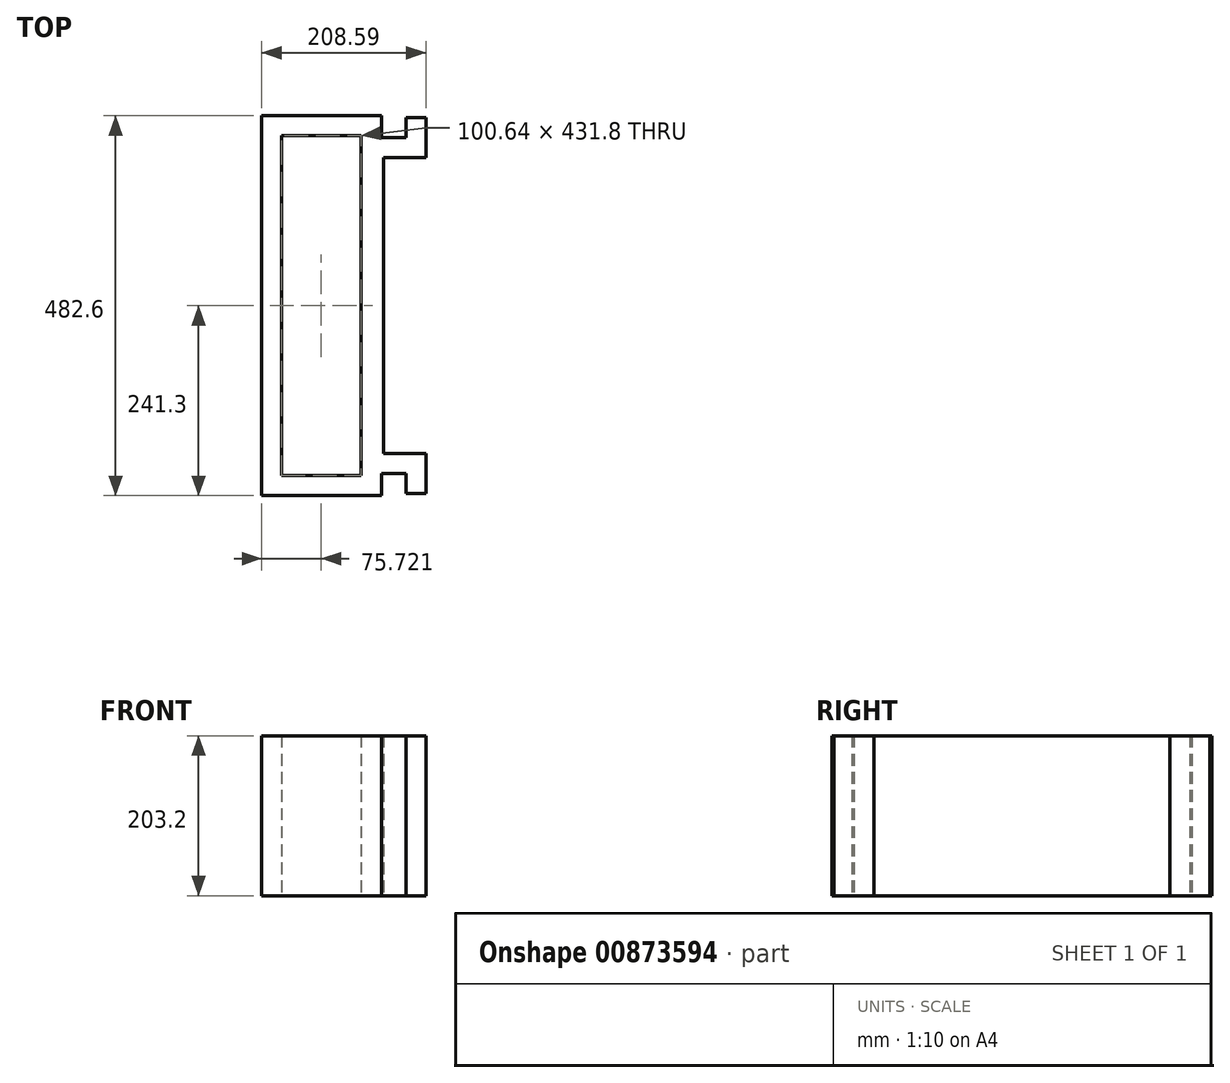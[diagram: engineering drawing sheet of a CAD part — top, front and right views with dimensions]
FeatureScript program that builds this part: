
annotation { "Feature Type Name" : "Feature", "Feature Type Description" : "" }
export const myFeature = defineFeature(function(context is Context, id is Id, definition is map)
    precondition{}
    {
        {
            var Q0;
            Q0=qCreatedBy(makeId("Top.planeOp"),FACE);
            var sketch = newSketch(context, id + "F0", { "sketchPlane" : qUnion([Q0])});
            skLineSegment(sketch, "E0.bottom", {"start": v(0, 0) * mm, "end": v(152.4, 0) * mm});
            skLineSegment(sketch, "E0.top", {"start": v(0, 482.6) * mm, "end": v(152.4, 482.6) * mm});
            skLineSegment(sketch, "E0.left", {"start": v(0, 0) * mm, "end": v(0, 482.6) * mm});
            skLineSegment(sketch, "E1", {"start": v(152.4, 482.6) * mm, "end": v(152.4, 457.2) * mm});
            skLineSegment(sketch, "E2", {"start": v(152.4, 0) * mm, "end": v(152.4, 25.4) * mm});
            skLineSegment(sketch, "E3", {"start": v(152.4, 457.2) * mm, "end": v(25.4, 457.2) * mm});
            skLineSegment(sketch, "E4", {"start": v(25.4, 457.2) * mm, "end": v(25.4, 25.4) * mm});
            skLineSegment(sketch, "E5", {"start": v(25.4, 25.4) * mm, "end": v(152.4, 25.4) * mm});
            skLineSegment(sketch, "E6.bottom", {"start": v(152.4, 457.2) * mm, "end": v(126.04, 457.2) * mm});
            skLineSegment(sketch, "E6.top", {"start": v(152.4, 454.66) * mm, "end": v(126.04, 454.66) * mm});
            skLineSegment(sketch, "E6.left", {"start": v(152.4, 457.2) * mm, "end": v(152.4, 454.66) * mm});
            skLineSegment(sketch, "E6.right", {"start": v(126.04, 457.2) * mm, "end": v(126.04, 454.66) * mm});
            skLineSegment(sketch, "E7.bottom", {"start": v(126.04, 454.66) * mm, "end": v(183.2, 454.66) * mm});
            skLineSegment(sketch, "E7.top", {"start": v(126.04, 429.26) * mm, "end": v(183.2, 429.26) * mm});
            skLineSegment(sketch, "E7.left", {"start": v(126.04, 454.66) * mm, "end": v(126.04, 429.26) * mm});
            skLineSegment(sketch, "E7.right", {"start": v(183.2, 454.66) * mm, "end": v(183.2, 429.26) * mm});
            skLineSegment(sketch, "E8.bottom", {"start": v(183.2, 429.26) * mm, "end": v(208.6, 429.26) * mm});
            skLineSegment(sketch, "E8.top", {"start": v(183.2, 480.06) * mm, "end": v(208.6, 480.06) * mm});
            skLineSegment(sketch, "E8.left", {"start": v(183.2, 429.26) * mm, "end": v(183.2, 480.06) * mm});
            skLineSegment(sketch, "E8.right", {"start": v(208.6, 429.26) * mm, "end": v(208.6, 480.06) * mm});
            skLineSegment(sketch, "E9", {"start": v(0, 241.3) * mm, "end": v(297.06, 241.3) * mm, "construction": true});
            skLineSegment(sketch, "E10.MirrorCS", {"start": v(126.04, 25.4) * mm, "end": v(126.04, 27.94) * mm});
            skLineSegment(sketch, "E11.MirrorCS", {"start": v(126.04, 27.94) * mm, "end": v(126.04, 53.34) * mm});
            skLineSegment(sketch, "E12.MirrorCS", {"start": v(126.04, 53.34) * mm, "end": v(183.2, 53.34) * mm});
            skLineSegment(sketch, "E13.MirrorCS", {"start": v(183.2, 53.34) * mm, "end": v(208.6, 53.34) * mm});
            skLineSegment(sketch, "E14.MirrorCS", {"start": v(208.6, 53.34) * mm, "end": v(208.6, 2.54) * mm});
            skLineSegment(sketch, "E15.MirrorCS", {"start": v(183.2, 2.54) * mm, "end": v(208.6, 2.54) * mm});
            skLineSegment(sketch, "E16.MirrorCS", {"start": v(183.2, 53.34) * mm, "end": v(183.2, 2.54) * mm});
            skLineSegment(sketch, "E17.MirrorCS", {"start": v(126.04, 27.94) * mm, "end": v(183.2, 27.94) * mm});
            skLineSegment(sketch, "E18.MirrorCS", {"start": v(152.4, 25.4) * mm, "end": v(152.4, 27.94) * mm});
            skLineSegment(sketch, "E19", {"start": v(126.04, 429.26) * mm, "end": v(126.04, 53.34) * mm});
            skLineSegment(sketch, "E20", {"start": v(154.62, 429.26) * mm, "end": v(154.62, 53.34) * mm});
            skSolve(sketch);
        }
        {
            var Q0;
            Q0 = qSketchRegion(id + "F0", true);
            extrude(context, id + "F1", {"entities" : qUnion([Q0]), "depth" : 203.2 * mm, "offsetDistance" : 25.4 * mm});
        }
    });
